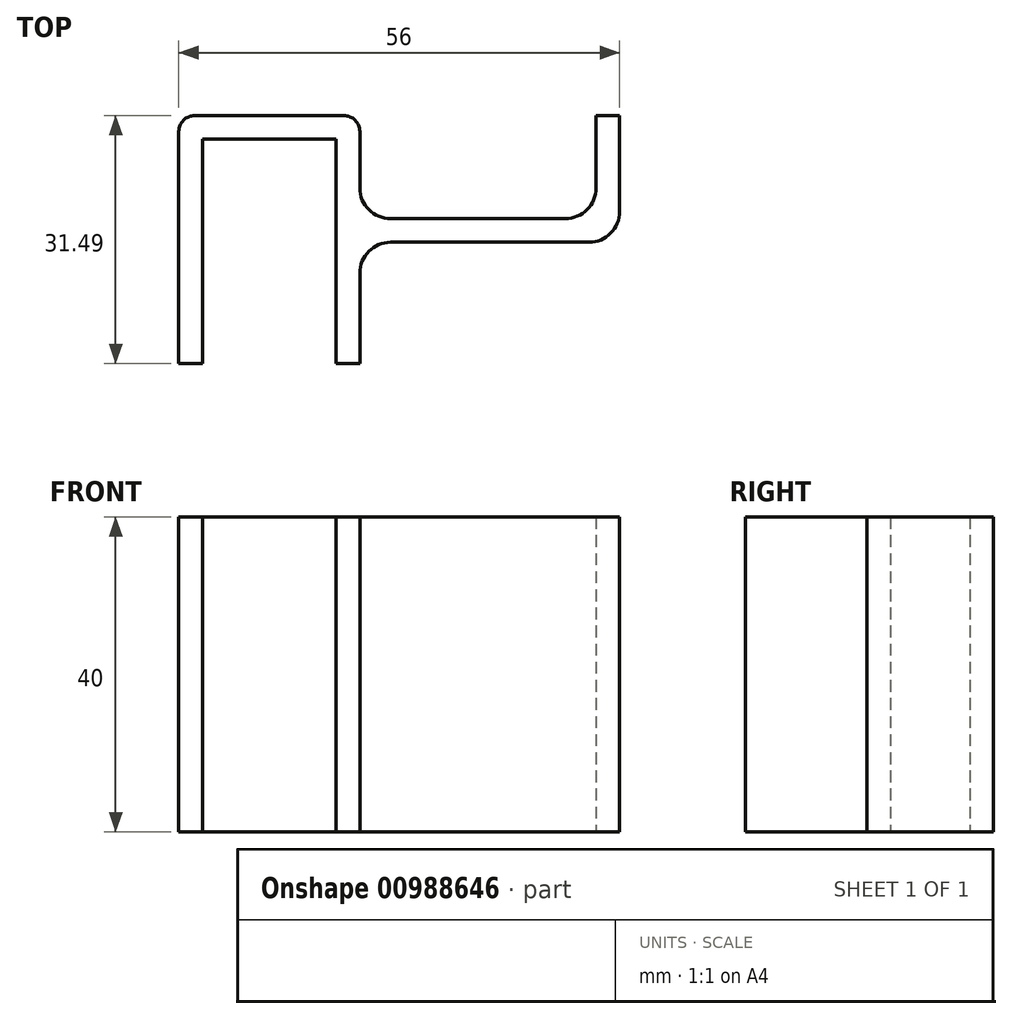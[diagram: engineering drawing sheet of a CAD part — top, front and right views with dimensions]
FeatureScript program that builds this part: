
annotation { "Feature Type Name" : "Feature", "Feature Type Description" : "" }
export const myFeature = defineFeature(function(context is Context, id is Id, definition is map)
    precondition{}
    {
        {
            var Q0;
            Q0=qCreatedBy(makeId("Top.planeOp"),FACE);
            var sketch = newSketch(context, id + "F0", { "sketchPlane" : qUnion([Q0])});
            skLineSegment(sketch, "E0", {"start": v(-53.13, -18.4) * mm, "end": v(-53.13, 11.09) * mm});
            skLineSegment(sketch, "E1", {"start": v(-51.13, 13.09) * mm, "end": v(-32.13, 13.09) * mm});
            skLineSegment(sketch, "E2", {"start": v(-30.13, -6.91) * mm, "end": v(-30.13, -18.4) * mm});
            skLineSegment(sketch, "E3", {"start": v(-30.13, -18.4) * mm, "end": v(-33.13, -18.4) * mm});
            skLineSegment(sketch, "E4", {"start": v(-33.13, -18.4) * mm, "end": v(-33.13, 10.09) * mm});
            skLineSegment(sketch, "E5", {"start": v(-33.13, 10.09) * mm, "end": v(-50.13, 10.09) * mm});
            skLineSegment(sketch, "E6", {"start": v(-50.13, 10.09) * mm, "end": v(-50.13, -18.4) * mm});
            skLineSegment(sketch, "E7", {"start": v(-50.13, -18.4) * mm, "end": v(-53.13, -18.4) * mm});
            skLineSegment(sketch, "E8", {"start": v(-26.21, 0) * mm, "end": v(-4.04, 0) * mm});
            skLineSegment(sketch, "E9", {"start": v(-0.13, 3.91) * mm, "end": v(-0.13, 13.09) * mm});
            skLineSegment(sketch, "E10", {"start": v(-0.13, 13.09) * mm, "end": v(2.87, 13.09) * mm});
            skLineSegment(sketch, "E11", {"start": v(2.87, 13.09) * mm, "end": v(2.87, 0.91) * mm});
            skLineSegment(sketch, "E12", {"start": v(-1.04, -3) * mm, "end": v(-26.21, -3) * mm});
            skPoint(sketch, "E13.newPointB", {"position": v(-30.13, -3) * mm});
            skArc(sketch, "E13.filletArc", {"start": v(-26.21, -3) * mm, "mid": v(-28.98, -4.15) * mm, "end": v(-30.13, -6.91) * mm});
            skLineSegment(sketch, "E14", {"start": v(-30.13, 3.91) * mm, "end": v(-30.13, 11.09) * mm});
            skPoint(sketch, "E15.visualSharp", {"position": v(-30.13, 0) * mm});
            skArc(sketch, "E15.filletArc", {"start": v(-30.13, 3.91) * mm, "mid": v(-28.98, 1.15) * mm, "end": v(-26.21, 0) * mm});
            skPoint(sketch, "E16.visualSharp", {"position": v(-0.13, 0) * mm});
            skArc(sketch, "E16.filletArc", {"start": v(-4.04, 0) * mm, "mid": v(-1.27, 1.15) * mm, "end": v(-0.13, 3.91) * mm});
            skPoint(sketch, "E17.visualSharp", {"position": v(2.87, -3) * mm});
            skArc(sketch, "E17.filletArc", {"start": v(-1.04, -3) * mm, "mid": v(1.73, -1.85) * mm, "end": v(2.87, 0.91) * mm});
            skPoint(sketch, "E18.visualSharp", {"position": v(-53.13, 13.09) * mm});
            skArc(sketch, "E18.filletArc", {"start": v(-51.13, 13.09) * mm, "mid": v(-52.54, 12.5) * mm, "end": v(-53.13, 11.09) * mm});
            skPoint(sketch, "E19.visualSharp", {"position": v(-30.13, 13.09) * mm});
            skArc(sketch, "E19.filletArc", {"start": v(-30.13, 11.09) * mm, "mid": v(-30.71, 12.5) * mm, "end": v(-32.13, 13.09) * mm});
            skSolve(sketch);
        }
        {
            var Q0;
            Q0=makeQuery(id+"F0.imprint","IMPRINT",FACE,{"disambiguationData":[TD([[makeQuery(id+"F0.imprint","IMPRINT",EDGE,{"derivedFrom":sQuery(id+"F0.wireOp",EDGE,"E0")}),-1.0]])]});
            extrude(context, id + "F1", {"entities" : qUnion([Q0]), "depth" : 40 * mm, "offsetDistance" : 25 * mm});
        }
    });
